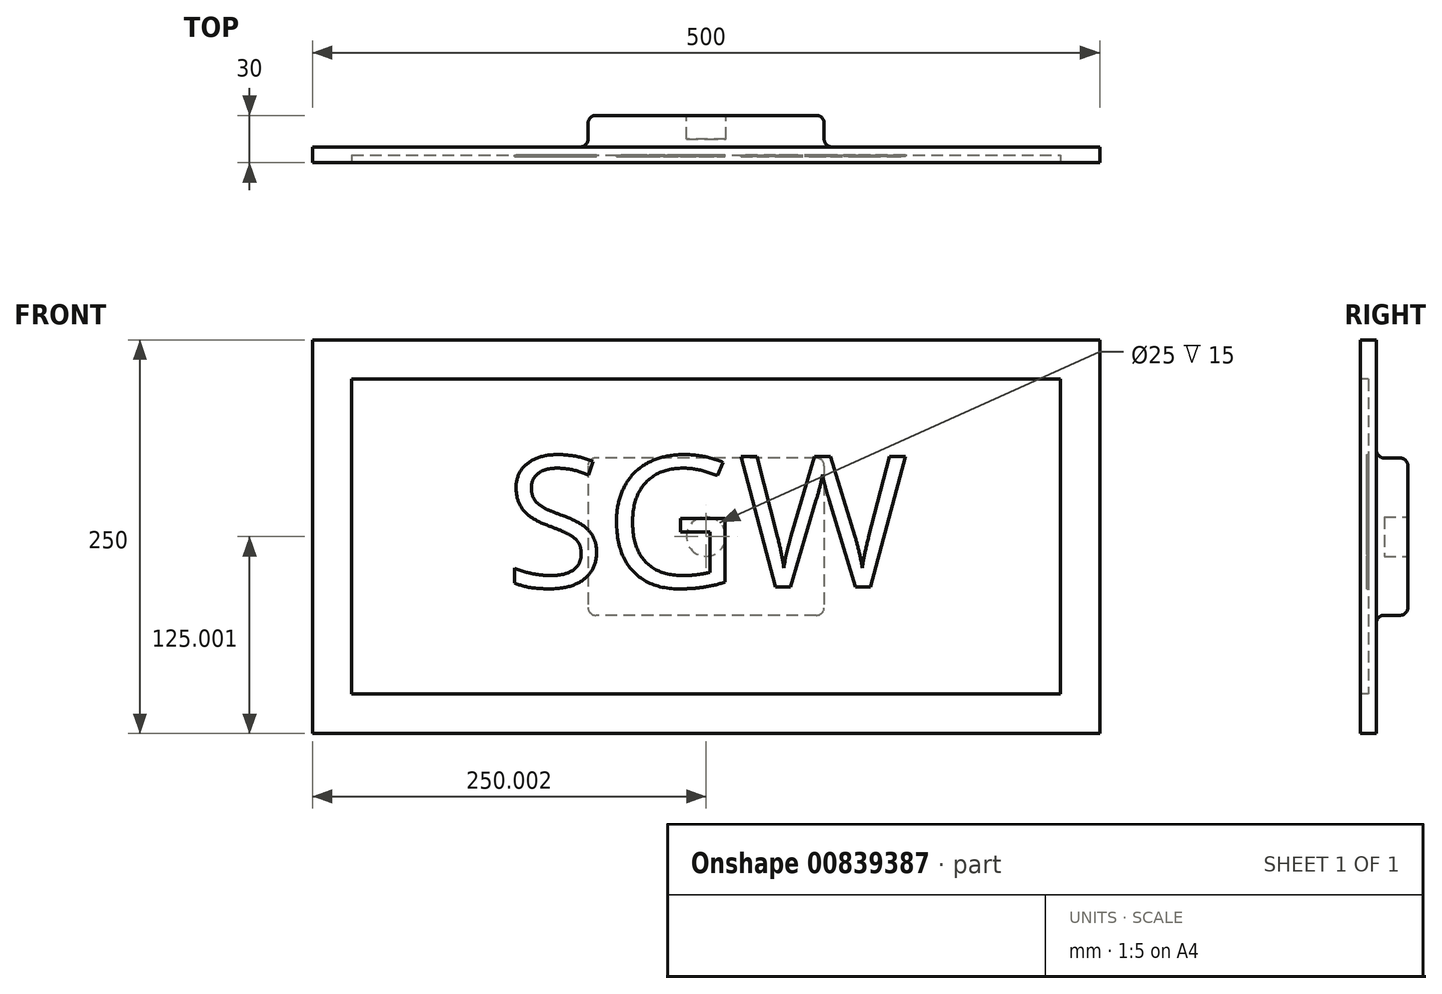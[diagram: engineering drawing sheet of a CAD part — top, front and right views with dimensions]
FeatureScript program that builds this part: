
annotation { "Feature Type Name" : "Feature", "Feature Type Description" : "" }
export const myFeature = defineFeature(function(context is Context, id is Id, definition is map)
    precondition{}
    {
        {
            var Q0;
            Q0=qCreatedBy(makeId("Front.planeOp"),FACE);
            var sketch = newSketch(context, id + "F0", { "sketchPlane" : qUnion([Q0])});
            skLineSegment(sketch, "E0.bottom", {"start": v(-224.54, 106.41) * mm, "end": v(275.46, 106.41) * mm});
            skLineSegment(sketch, "E0.top", {"start": v(-224.54, -143.59) * mm, "end": v(275.46, -143.59) * mm});
            skLineSegment(sketch, "E0.left", {"start": v(-224.54, 106.41) * mm, "end": v(-224.54, -143.59) * mm});
            skLineSegment(sketch, "E0.right", {"start": v(275.46, 106.41) * mm, "end": v(275.46, -143.59) * mm});
            skSolve(sketch);
        }
        {
            var Q0;
            Q0=makeQuery(id+"F0.imprint","IMPRINT",FACE,{"disambiguationData":[TD([[makeQuery(id+"F0.imprint","IMPRINT",EDGE,{"derivedFrom":sQuery(id+"F0.wireOp",EDGE,"E0.bottom")}),-1.0]])]});
            extrude(context, id + "F1", {"entities" : qUnion([Q0]), "depth" : 10 * mm, "offsetDistance" : 25 * mm});
        }
        {
            var Q0;
            Q0=makeQuery(id+"F1.opExtrude","CAP_FACE",FACE,{"disambiguationData":[OSD([sQuery(id+"F0.wireOp",EDGE,"E0.bottom"),sQuery(id+"F0.wireOp",EDGE,"E0.top"),sQuery(id+"F0.wireOp",EDGE,"E0.left"),sQuery(id+"F0.wireOp",EDGE,"E0.right")])],"isStart":false});
            var sketch = newSketch(context, id + "F2", { "sketchPlane" : qUnion([Q0])});
            skLineSegment(sketch, "E1.bottom", {"start": v(-199.54, 81.41) * mm, "end": v(250.46, 81.41) * mm});
            skLineSegment(sketch, "E1.top", {"start": v(-199.54, -118.59) * mm, "end": v(250.46, -118.59) * mm});
            skLineSegment(sketch, "E1.left", {"start": v(-199.54, 81.41) * mm, "end": v(-199.54, -118.59) * mm});
            skLineSegment(sketch, "E1.right", {"start": v(250.46, 81.41) * mm, "end": v(250.46, -118.59) * mm});
            skSolve(sketch);
        }
        {
            var Q0;
            Q0=makeQuery(id+"F2.imprint","IMPRINT",FACE,{"disambiguationData":[TD([[makeQuery(id+"F2.imprint","IMPRINT",EDGE,{"derivedFrom":sQuery(id+"F2.wireOp",EDGE,"E1.bottom")}),-1.0]])]});
            extrude(context, id + "F3", {"entities" : qUnion([Q0]), "operationType" : NewBodyOperationType.REMOVE, "oppositeDirection" : true, "depth" : 5 * mm, "offsetDistance" : 25 * mm});
        }
        {
            var Q0;
            Q0=makeQuery(id+"F1.opExtrude","CAP_FACE",FACE,{"disambiguationData":[OSD([sQuery(id+"F0.wireOp",EDGE,"E0.bottom"),sQuery(id+"F0.wireOp",EDGE,"E0.top"),sQuery(id+"F0.wireOp",EDGE,"E0.left"),sQuery(id+"F0.wireOp",EDGE,"E0.right")])],"isStart":true});
            var sketch = newSketch(context, id + "F4", { "sketchPlane" : qUnion([Q0])});
            skLineSegment(sketch, "E2.bottom", {"start": v(-100.46, 31.41) * mm, "end": v(49.54, 31.41) * mm});
            skLineSegment(sketch, "E2.top", {"start": v(-100.46, -68.59) * mm, "end": v(49.54, -68.59) * mm});
            skLineSegment(sketch, "E2.left", {"start": v(-100.46, 31.41) * mm, "end": v(-100.46, -68.59) * mm});
            skLineSegment(sketch, "E2.right", {"start": v(49.54, 31.41) * mm, "end": v(49.54, -68.59) * mm});
            skSolve(sketch);
        }
        {
            var Q0;
            Q0=makeQuery(id+"F4.imprint","IMPRINT",FACE,{"disambiguationData":[TD([[makeQuery(id+"F4.imprint","IMPRINT",EDGE,{"derivedFrom":sQuery(id+"F4.wireOp",EDGE,"E2.bottom")}),-1.0]])]});
            extrude(context, id + "F5", {"entities" : qUnion([Q0]), "operationType" : NewBodyOperationType.ADD, "depth" : 20 * mm, "offsetDistance" : 25 * mm});
        }
        {
            var Q0;
            Q0=makeQuery(id+"F5.opExtrude","CAP_FACE",FACE,{"disambiguationData":[OSD([sQuery(id+"F4.wireOp",EDGE,"E2.bottom"),sQuery(id+"F4.wireOp",EDGE,"E2.top"),sQuery(id+"F4.wireOp",EDGE,"E2.left"),sQuery(id+"F4.wireOp",EDGE,"E2.right")])],"isStart":false});
            var sketch = newSketch(context, id + "F6", { "sketchPlane" : qUnion([Q0])});
            skCircle(sketch, "E3", {"center": v(-25.46, -18.59) * mm, "radius": 12.5 * mm});
            skSolve(sketch);
        }
        {
            var Q0;
            Q0=makeQuery(id+"F6.imprint","IMPRINT",FACE,{"disambiguationData":[TD([[makeQuery(id+"F6.imprint","IMPRINT",EDGE,{"derivedFrom":sQuery(id+"F6.wireOp",EDGE,"E3")}),1.0]])]});
            extrude(context, id + "F7", {"entities" : qUnion([Q0]), "operationType" : NewBodyOperationType.REMOVE, "oppositeDirection" : true, "depth" : 15 * mm, "offsetDistance" : 25 * mm});
        }
        {
            var Q0;
            Q0=makeQuery(id+"F5.opExtrude","SWEPT_FACE",FACE,{"disambiguationData":[OSD([sQuery(id+"F4.wireOp",EDGE,"E2.left")])]});
            var Q1;
            Q1=makeQuery(id+"F5.opExtrude","SWEPT_FACE",FACE,{"disambiguationData":[OSD([sQuery(id+"F4.wireOp",EDGE,"E2.bottom")])]});
            var Q2;
            Q2=makeQuery(id+"F5.opExtrude","SWEPT_FACE",FACE,{"disambiguationData":[OSD([sQuery(id+"F4.wireOp",EDGE,"E2.right")])]});
            var Q3;
            Q3=makeQuery(id+"F5.opExtrude","SWEPT_FACE",FACE,{"disambiguationData":[OSD([sQuery(id+"F4.wireOp",EDGE,"E2.top")])]});
            fillet(context, id + "F8", {"entities" : qUnion([Q0, Q1, Q2, Q3]), "radius" : 5 * mm, "tangentPropagation" : true, "allowEdgeOverflow" : false});
        }
        {
            var Q0;
            Q0=makeQuery(id+"F3.boolean.opBoolean","COPY",FACE,{"derivedFrom":makeQuery(id+"F3.opExtrude","CAP_FACE",FACE,{"disambiguationData":[OSD([sQuery(id+"F2.wireOp",EDGE,"E1.bottom"),sQuery(id+"F2.wireOp",EDGE,"E1.top"),sQuery(id+"F2.wireOp",EDGE,"E1.left"),sQuery(id+"F2.wireOp",EDGE,"E1.right")])],"isStart":false})});
            var sketch = newSketch(context, id + "F9", { "sketchPlane" : qUnion([Q0])});
            skText(sketch, "E4", { "text": "SGW", "fontName": "OpenSans-Regular.ttf"});
            const initialGuessF9  = {"E4": [-0.10231, -0.05061, 1, 0, 0.08366]};
            skSetInitialGuess(sketch, initialGuessF9);
            skSolve(sketch);
        }
        {
            var Q0;
            Q0 = qSketchRegion(id + "F9", true);
            extrude(context, id + "F10", {"entities" : qUnion([Q0]), "operationType" : NewBodyOperationType.ADD, "depth" : 1 * mm, "offsetDistance" : 25 * mm});
        }
    });
